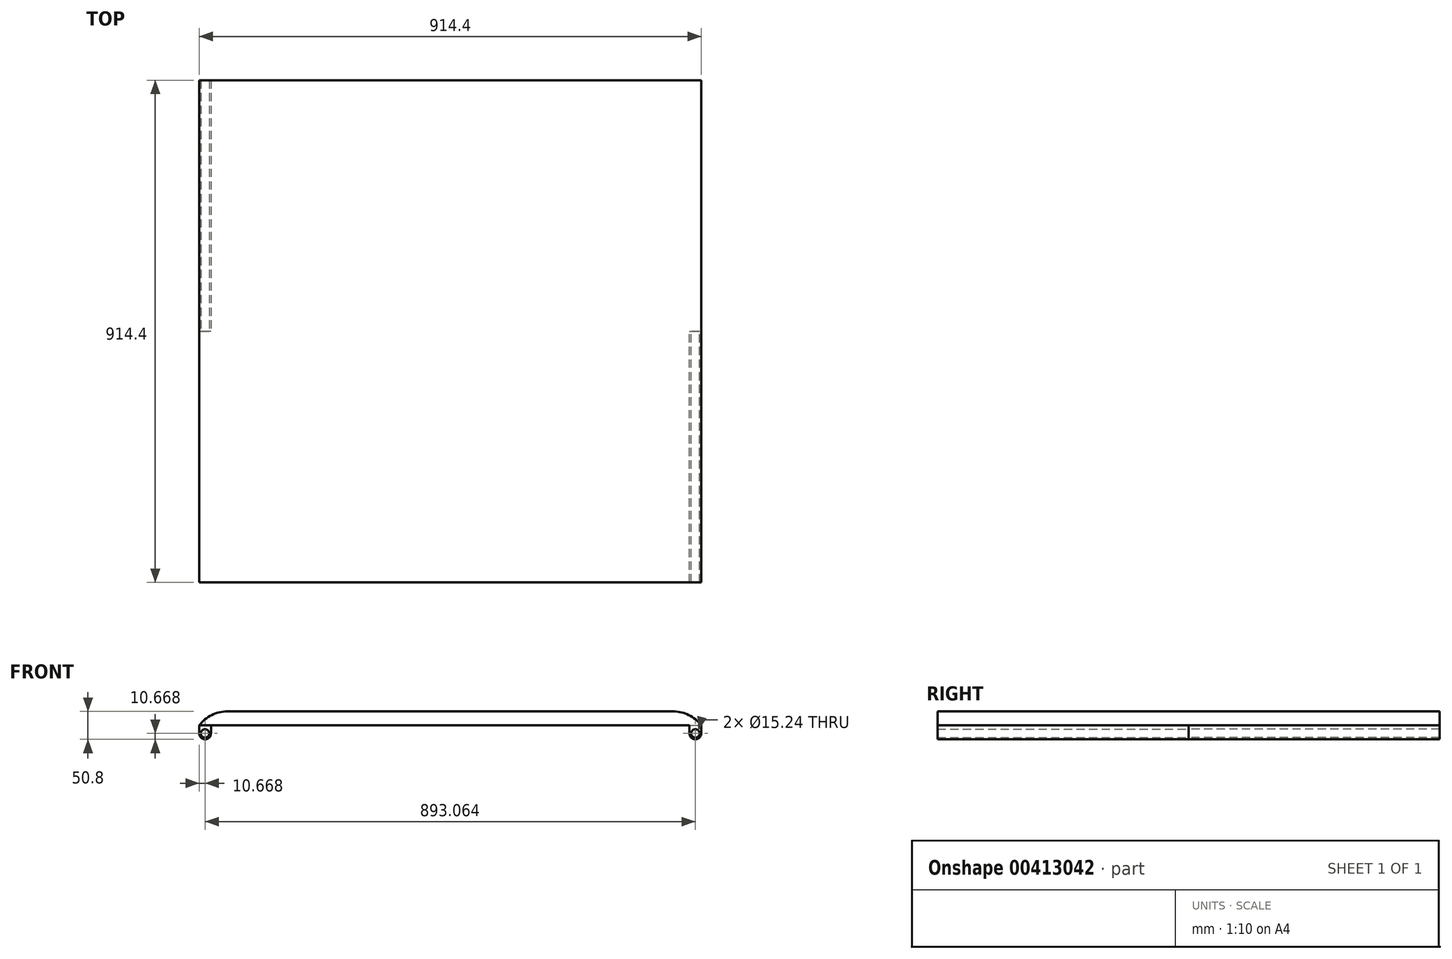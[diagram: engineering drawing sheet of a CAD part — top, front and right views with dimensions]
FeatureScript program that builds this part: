
annotation { "Feature Type Name" : "Feature", "Feature Type Description" : "" }
export const myFeature = defineFeature(function(context is Context, id is Id, definition is map)
    precondition{}
    {
        {
            var Q0;
            Q0=qCreatedBy(makeId("Top.planeOp"),FACE);
            cPlane(context, id + "F0", {"entities" : qUnion([Q0]), "cplaneType" : CPlaneType.OFFSET, "offset" : 914.4 * mm, "width" : 152.4 * mm, "height" : 152.4 * mm});
        }
        {
            var Q0;
            Q0=qCreatedBy(id+"F0.planeOp",FACE);
            var sketch = newSketch(context, id + "F1", { "sketchPlane" : qUnion([Q0])});
            skLineSegment(sketch, "E0.bottom", {"start": v(457.2, -457.2) * mm, "end": v(-457.2, -457.2) * mm});
            skLineSegment(sketch, "E0.top", {"start": v(457.2, 457.2) * mm, "end": v(-457.2, 457.2) * mm});
            skLineSegment(sketch, "E0.left", {"start": v(457.2, -457.2) * mm, "end": v(457.2, 457.2) * mm});
            skLineSegment(sketch, "E0.right", {"start": v(-457.2, -457.2) * mm, "end": v(-457.2, 457.2) * mm});
            skPoint(sketch, "E0.middle", {"position": v(0, 0) * mm});
            skSolve(sketch);
        }
        {
            var Q0;
            Q0=makeQuery(id+"F1.imprint","IMPRINT",FACE,{"disambiguationData":[TD([[makeQuery(id+"F1.imprint","IMPRINT",EDGE,{"derivedFrom":sQuery(id+"F1.wireOp",EDGE,"E0.bottom")}),-1.0]])]});
            extrude(context, id + "F2", {"entities" : qUnion([Q0]), "oppositeDirection" : true, "depth" : 25.4 * mm});
        }
        {
            var Q0;
            Q0=makeQuery(id+"F2.opExtrude","SWEPT_FACE",FACE,{"disambiguationData":[OSD([sQuery(id+"F1.wireOp",EDGE,"E0.bottom")])]});
            var sketch = newSketch(context, id + "F3", { "sketchPlane" : qUnion([Q0])});
            skArc(sketch, "E1", {"start": v(-405.85, 914.4) * mm, "mid": v(-434.5, 907.7) * mm, "end": v(-457.2, 889) * mm});
            skLineSegment(sketch, "E2", {"start": v(0, 270.7) * mm, "end": v(0, 1167.33) * mm, "construction": true});
            skLineSegment(sketch, "E3", {"start": v(-405.85, 914.4) * mm, "end": v(-457.2, 914.4) * mm});
            skLineSegment(sketch, "E4", {"start": v(-457.2, 914.4) * mm, "end": v(-457.2, 889) * mm});
            skLineSegment(sketch, "E5.MirrorCS", {"start": v(457.2, 914.4) * mm, "end": v(457.2, 889) * mm});
            skArc(sketch, "E6.MirrorCS", {"start": v(405.85, 914.4) * mm, "mid": v(434.5, 907.7) * mm, "end": v(457.2, 889) * mm});
            skLineSegment(sketch, "E7.MirrorCS", {"start": v(405.85, 914.4) * mm, "end": v(457.2, 914.4) * mm});
            skSolve(sketch);
        }
        {
            var Q0;
            Q0 = qSketchRegion(id + "F3", true);
            var Q1;
            Q1=makeQuery(id+"F2.opExtrude","SWEPT_FACE",FACE,{"disambiguationData":[OSD([sQuery(id+"F1.wireOp",EDGE,"E0.top")])]});
            extrude(context, id + "F4", {"entities" : qUnion([Q0]), "operationType" : NewBodyOperationType.REMOVE, "endBound" : BoundingType.UP_TO_SURFACE, "oppositeDirection" : true, "endBoundEntityFace" : qUnion([Q1]), "depth" : 30.48 * mm});
        }
        {
            var Q0;
            Q0=makeQuery(id+"F2.opExtrude","CAP_FACE",FACE,{"disambiguationData":[OSD([sQuery(id+"F1.wireOp",EDGE,"E0.bottom"),sQuery(id+"F1.wireOp",EDGE,"E0.top"),sQuery(id+"F1.wireOp",EDGE,"E0.left"),sQuery(id+"F1.wireOp",EDGE,"E0.right")])],"isStart":false});
            var sketch = newSketch(context, id + "F5", { "sketchPlane" : qUnion([Q0])});
            skLineSegment(sketch, "E8", {"start": v(-457.2, 0) * mm, "end": v(457.2, 0) * mm, "construction": true});
            skSolve(sketch);
        }
        {
            var Q0;
            Q0=qCreatedBy(makeId("Front.planeOp"),FACE);
            var sketch = newSketch(context, id + "F6", { "sketchPlane" : qUnion([Q0])});
            skArc(sketch, "E9", {"start": v(-457.2, 874.27) * mm, "mid": v(-446.53, 863.6) * mm, "end": v(-435.86, 874.27) * mm});
            skLineSegment(sketch, "E10", {"start": v(-446.53, 863.6) * mm, "end": v(-753.6, 863.6) * mm, "construction": true});
            skLineSegment(sketch, "E11", {"start": v(-457.2, 889) * mm, "end": v(-457.2, 832.91) * mm, "construction": true});
            skCircle(sketch, "E12.0", {"center": v(-446.53, 874.27) * mm, "radius": 7.62 * mm});
            skLineSegment(sketch, "E13", {"start": v(-435.86, 874.27) * mm, "end": v(-435.86, 889) * mm});
            skLineSegment(sketch, "E14", {"start": v(-435.86, 889) * mm, "end": v(-457.2, 889) * mm});
            skLineSegment(sketch, "E15", {"start": v(-457.2, 889) * mm, "end": v(-457.2, 872.84) * mm});
            skLineSegment(sketch, "E16", {"start": v(0, 888.67) * mm, "end": v(0, 607.24) * mm, "construction": true});
            skLineSegment(sketch, "E17.MirrorCS", {"start": v(435.86, 874.27) * mm, "end": v(435.86, 889) * mm});
            skLineSegment(sketch, "E18.MirrorCS", {"start": v(446.53, 863.6) * mm, "end": v(753.6, 863.6) * mm, "construction": true});
            skLineSegment(sketch, "E19.MirrorCS", {"start": v(457.2, 889) * mm, "end": v(457.2, 872.84) * mm});
            skLineSegment(sketch, "E20.MirrorCS", {"start": v(435.86, 889) * mm, "end": v(457.2, 889) * mm});
            skArc(sketch, "E21.MirrorCS", {"start": v(457.2, 874.27) * mm, "mid": v(446.53, 863.6) * mm, "end": v(435.86, 874.27) * mm});
            skCircle(sketch, "E22.MirrorC", {"center": v(446.53, 874.27) * mm, "radius": 7.62 * mm});
            skSolve(sketch);
        }
        {
            var Q0;
            {var subQ1=sQuery(id+"F6.wireOp",EDGE,"E9");Q0=makeQuery(id+"F6.imprint","IMPRINT",FACE,{"disambiguationData":[TD([[makeQuery(id+"F6.imprint","IMPRINT",EDGE,{"derivedFrom":subQ1}),1.0]])]});}
            var Q1;
            {var subQ0=sQuery(id+"F1.wireOp",EDGE,"E0.top");Q1=makeQuery(id+"F4.boolean.opBoolean","MERGE",VERTEX,{"derivedFrom":[makeQuery(id+"F2.opExtrude","CAP_VERTEX",VERTEX,{"disambiguationData":[OSD([subQ0,sQuery(id+"F1.wireOp",EDGE,"E0.right")])],"isStart":false}),makeQuery(id+"F4.opExtrude","CAP_VERTEX",VERTEX,{"disambiguationData":[OSD([sQuery(id+"F1.wireOp",EDGE,"E0.bottom"),subQ0,sQuery(id+"F3.wireOp",EDGE,"E1"),sQuery(id+"F3.wireOp",EDGE,"E4")])],"isStart":false})]});}
            extrude(context, id + "F7", {"entities" : qUnion([Q0]), "operationType" : NewBodyOperationType.ADD, "endBound" : BoundingType.UP_TO_VERTEX, "oppositeDirection" : true, "endBoundEntityVertex" : qUnion([Q1]), "depth" : 30.48 * mm});
        }
        {
            var Q0;
            Q0=makeQuery(id+"F6.imprint","IMPRINT",FACE,{"disambiguationData":[TD([[makeQuery(id+"F6.imprint","IMPRINT",EDGE,{"derivedFrom":sQuery(id+"F6.wireOp",EDGE,"E17.MirrorCS")}),-1.0]])]});
            var Q1;
            {var subQ0=sQuery(id+"F1.wireOp",EDGE,"E0.bottom");Q1=makeQuery(id+"F4.boolean.opBoolean","MERGE",VERTEX,{"derivedFrom":[makeQuery(id+"F2.opExtrude","CAP_VERTEX",VERTEX,{"disambiguationData":[OSD([subQ0,sQuery(id+"F1.wireOp",EDGE,"E0.left")])],"isStart":false}),makeQuery(id+"F4.opExtrude","CAP_VERTEX",VERTEX,{"disambiguationData":[OSD([subQ0,sQuery(id+"F3.wireOp",EDGE,"E5.MirrorCS"),sQuery(id+"F3.wireOp",EDGE,"E6.MirrorCS")])],"isStart":true})]});}
            extrude(context, id + "F8", {"entities" : qUnion([Q0]), "operationType" : NewBodyOperationType.ADD, "endBound" : BoundingType.UP_TO_VERTEX, "endBoundEntityVertex" : qUnion([Q1]), "depth" : 30.48 * mm});
        }
    });
